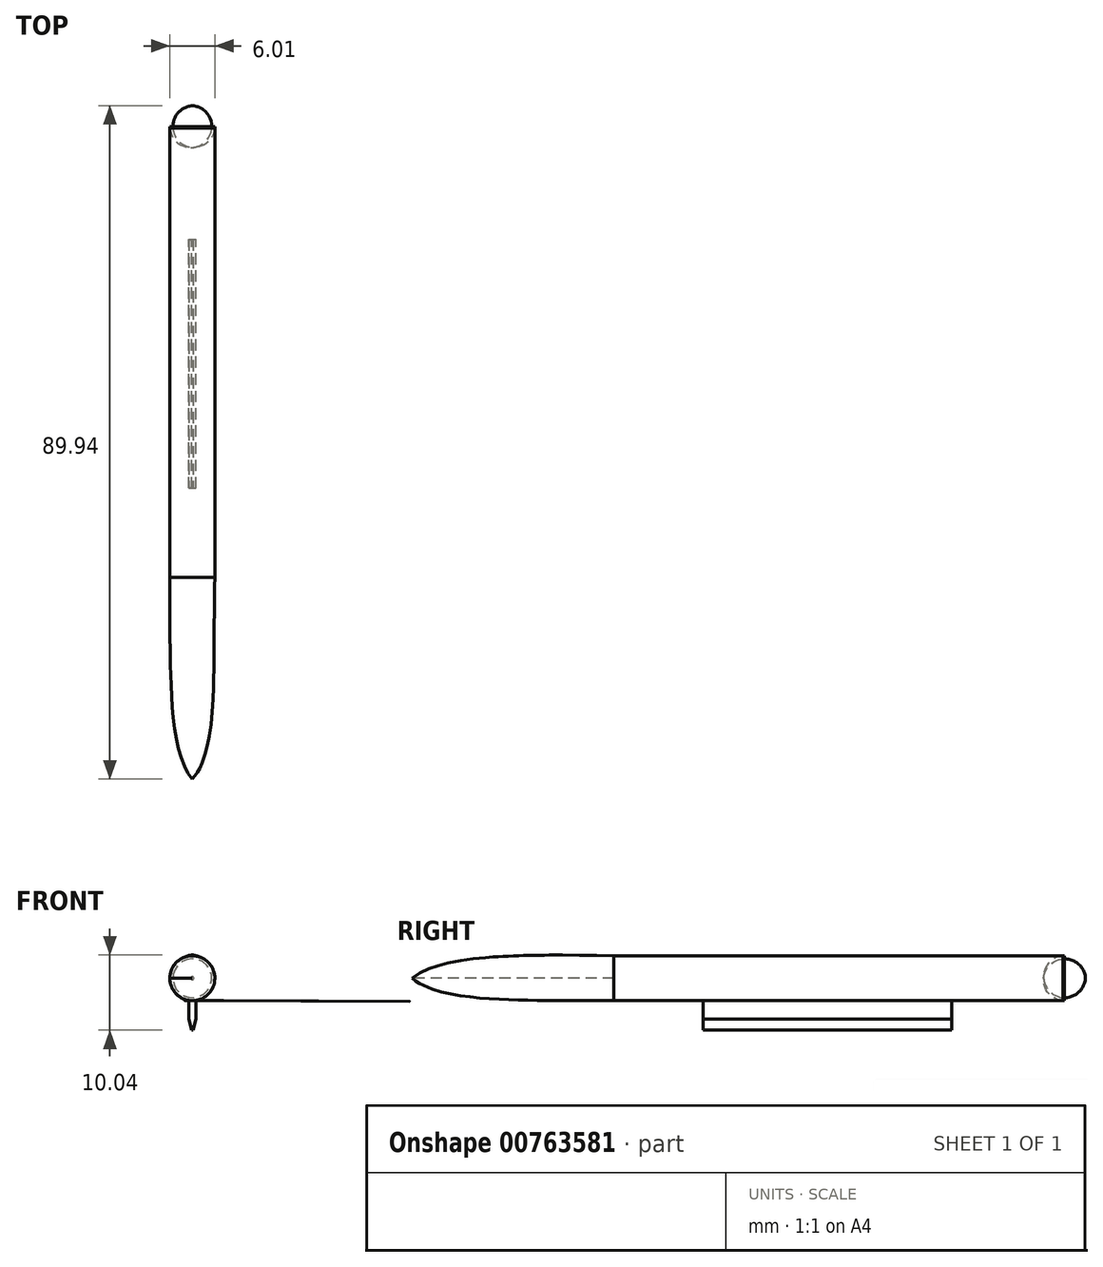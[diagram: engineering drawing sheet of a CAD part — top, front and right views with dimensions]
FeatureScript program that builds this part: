
annotation { "Feature Type Name" : "Feature", "Feature Type Description" : "" }
export const myFeature = defineFeature(function(context is Context, id is Id, definition is map)
    precondition{}
    {
        {
            var Q0;
            Q0=qCreatedBy(makeId("Front.planeOp"),FACE);
            var sketch = newSketch(context, id + "F0", { "sketchPlane" : qUnion([Q0])});
            skCircle(sketch, "E0", {"center": v(0, 0) * mm, "radius": 3 * mm});
            skSolve(sketch);
        }
        {
            var Q0;
            Q0=qCreatedBy(makeId("Front.planeOp"),FACE);
            cPlane(context, id + "F1", {"entities" : qUnion([Q0]), "cplaneType" : CPlaneType.OFFSET, "offset" : 60 * mm, "width" : 150 * mm, "height" : 150 * mm});
        }
        {
            var Q0;
            Q0=qCreatedBy(id+"F1.planeOp",FACE);
            var sketch = newSketch(context, id + "F2", { "sketchPlane" : qUnion([Q0])});
            skCircle(sketch, "E1", {"center": v(0, 0) * mm, "radius": 3 * mm});
            skSolve(sketch);
        }
        {
            var Q0;
            Q0=sQuery(id+"F0.wireOp",EDGE,"E0");
            extrude(context, id + "F3", {"bodyType" : ToolBodyType.SURFACE, "surfaceEntities" : qUnion([Q0]), "depth" : 60 * mm, "offsetDistance" : 25 * mm});
        }
        {
            var Q0;
            Q0=makeQuery(id+"F2.imprint","IMPRINT",FACE,{"disambiguationData":[TD([[makeQuery(id+"F2.imprint","IMPRINT",EDGE,{"derivedFrom":sQuery(id+"F2.wireOp",EDGE,"E1")}),1.0]])]});
            var sketch = newSketch(context, id + "F4", { "sketchPlane" : qUnion([Q0])});
            skPoint(sketch, "E2", {"position": v(3, 0) * mm});
            skPoint(sketch, "E3", {"position": v(-3, 0) * mm});
            skPoint(sketch, "E4", {"position": v(0, -3) * mm});
            skPoint(sketch, "E5", {"position": v(0, 3) * mm});
            skSolve(sketch);
        }
        {
            var Q0;
            Q0=qCreatedBy(makeId("Top.planeOp"),FACE);
            var sketch = newSketch(context, id + "F5", { "sketchPlane" : qUnion([Q0])});
            skFitSpline(sketch, "E6", {"points": [v(-3, -60) * mm, v(-2.94, -70.93) * mm, v(0, -86.94) * mm], "startDerivative": vector(-0.08, -29.66) * mm, "endDerivative": vector(14.32, -16.3) * mm});
            skFitSpline(sketch, "E7", {"points": [v(0, -86.94) * mm, v(2.9, -71.06) * mm, v(3, -60) * mm], "startDerivative": vector(15.12, 16.21) * mm, "endDerivative": vector(0.48, 29.25) * mm});
            skSolve(sketch);
        }
        {
            var Q0;
            Q0=qCreatedBy(makeId("Right.planeOp"),FACE);
            var sketch = newSketch(context, id + "F6", { "sketchPlane" : qUnion([Q0])});
            skFitSpline(sketch, "E8", {"points": [v(-60, -3) * mm, v(-71.3, -2.94) * mm, v(-86.94, 0) * mm], "startDerivative": vector(-34.6, 0.4) * mm, "endDerivative": vector(-15.88, 14.42) * mm});
            skFitSpline(sketch, "E9", {"points": [v(-86.94, 0) * mm, v(-71.31, 3.04) * mm, v(-60, 3) * mm], "startDerivative": vector(16.22, 14.34) * mm, "endDerivative": vector(34, -0.55) * mm});
            skSolve(sketch);
        }
        {
            var Q0;
            Q0=makeQuery(id+"F2.imprint","IMPRINT",FACE,{"disambiguationData":[TD([[makeQuery(id+"F2.imprint","IMPRINT",EDGE,{"derivedFrom":sQuery(id+"F2.wireOp",EDGE,"E1")}),1.0]])]});
            var Q1;
            Q1=sQuery(id+"F6.wireOp",VERTEX,"E9.0.internal");
            var Q2;
            Q2=sQuery(id+"F5.wireOp",EDGE,"E6");
            var Q3;
            Q3=sQuery(id+"F5.wireOp",EDGE,"E7");
            var Q4;
            Q4=sQuery(id+"F6.wireOp",EDGE,"E8");
            var Q5;
            Q5=sQuery(id+"F6.wireOp",EDGE,"E9");
            loft(context, id + "F7", {"addGuides" : true, "sheetProfilesArray" : [{ "sheetProfileEntities" : qUnion([Q0]) }, { "sheetProfileEntities" : qUnion([Q1]) }], "guidesArray" : [{ "guideEntities" : qUnion([Q2]), "guideDerivativeType" : LoftGuideDerivativeType.DEFAULT, "guideDerivativeMagnitude" : 1 }, { "guideEntities" : qUnion([Q3]), "guideDerivativeType" : LoftGuideDerivativeType.DEFAULT, "guideDerivativeMagnitude" : 1 }, { "guideEntities" : qUnion([Q4]), "guideDerivativeType" : LoftGuideDerivativeType.DEFAULT, "guideDerivativeMagnitude" : 1 }, { "guideEntities" : qUnion([Q5]), "guideDerivativeType" : LoftGuideDerivativeType.DEFAULT, "guideDerivativeMagnitude" : 1 }]});
        }
        {
            var Q0;
            Q0=qCreatedBy(makeId("Right.planeOp"),FACE);
            var sketch = newSketch(context, id + "F8", { "sketchPlane" : qUnion([Q0])});
            skLineSegment(sketch, "E10.bottom", {"start": v(-48.1, -2.93) * mm, "end": v(-14.87, -2.94) * mm});
            skLineSegment(sketch, "E10.top", {"start": v(-48.1, -6.93) * mm, "end": v(-14.9, -6.94) * mm});
            skLineSegment(sketch, "E10.left", {"start": v(-48.1, -6.93) * mm, "end": v(-48.1, -2.93) * mm});
            skLineSegment(sketch, "E10.right", {"start": v(-14.9, -6.94) * mm, "end": v(-14.87, -2.94) * mm});
            skSolve(sketch);
        }
        {
            var Q0;
            Q0=makeQuery(id+"F8.imprint","IMPRINT",FACE,{"disambiguationData":[TD([[makeQuery(id+"F8.imprint","IMPRINT",EDGE,{"derivedFrom":sQuery(id+"F8.wireOp",EDGE,"E10.bottom")}),-1.0]])]});
            extrude(context, id + "F9", {"entities" : qUnion([Q0]), "depth" : 1 * mm, "offsetDistance" : 25 * mm, "symmetric" : true});
        }
        {
            var Q0;
            Q0=makeQuery(id+"F9.opExtrude","CAP_EDGE",EDGE,{"disambiguationData":[OSD([sQuery(id+"F8.wireOp",EDGE,"E10.top")])],"isStart":false});
            var Q1;
            Q1=makeQuery(id+"F9.opExtrude","CAP_EDGE",EDGE,{"disambiguationData":[OSD([sQuery(id+"F8.wireOp",EDGE,"E10.top")])],"isStart":true});
            chamfer(context, id + "F10", {"entities" : qUnion([Q0, Q1]), "chamferType" : ChamferType.OFFSET_ANGLE, "width" : 1.5 * mm, "oppositeDirection" : false, "angle" : 15 * degree, "tangentPropagation" : true});
        }
        {
            var Q0;
            Q0=makeQuery(id+"FlL8xsbAWAlsFt4_0.boolean.opBoolean","MERGE",FACE,{"derivedFrom":[makeQuery(id+"F9.opExtrude","SWEPT_FACE",FACE,{"disambiguationData":[OSD([sQuery(id+"F8.wireOp",EDGE,"E10.right")])]}),makeQuery(id+"FlL8xsbAWAlsFt4_0.opExtrude","CAP_FACE",FACE,{"disambiguationData":[OSD([sQuery(id+"F0.wireOp",EDGE,"E0")])],"isStart":true})]});
            var sketch = newSketch(context, id + "F11", { "sketchPlane" : qUnion([Q0])});
            skCircle(sketch, "E11", {"center": v(0, 0) * mm, "radius": 3 * mm});
            skSolve(sketch);
        }
        {
            var Q0;
            Q0=makeQuery(id+"F0.imprint","IMPRINT",FACE,{"disambiguationData":[TD([[makeQuery(id+"F0.imprint","IMPRINT",EDGE,{"derivedFrom":sQuery(id+"F0.wireOp",EDGE,"E0")}),1.0]])]});
            extrude(context, id + "F12", {"entities" : qUnion([Q0]), "operationType" : NewBodyOperationType.ADD, "depth" : 60 * mm, "offsetDistance" : 25 * mm});
        }
        {
            var Q0;
            Q0=makeQuery(id+"F12.opExtrude","CAP_FACE",FACE,{"disambiguationData":[OSD([sQuery(id+"F0.wireOp",EDGE,"E0")])],"isStart":true});
            extrude(context, id + "F13", {"entities" : qUnion([Q0]), "depth" : 3 * mm, "offsetDistance" : 25 * mm});
        }
        {
            var Q0;
            Q0=makeQuery(id+"F13.opExtrude","CAP_FACE",FACE,{"disambiguationData":[OSD([sQuery(id+"F0.wireOp",EDGE,"E0")])],"isStart":false});
            var Q1;
            Q1=makeQuery(id+"F13.opExtrude","CAP_FACE",FACE,{"disambiguationData":[OSD([sQuery(id+"F11.wireOp",EDGE,"E11")])],"isStart":false});
            fillet(context, id + "F14", {"entities" : qUnion([Q0, Q1]), "radius" : 2.8 * mm, "tangentPropagation" : true, "allowEdgeOverflow" : false});
        }
    });
